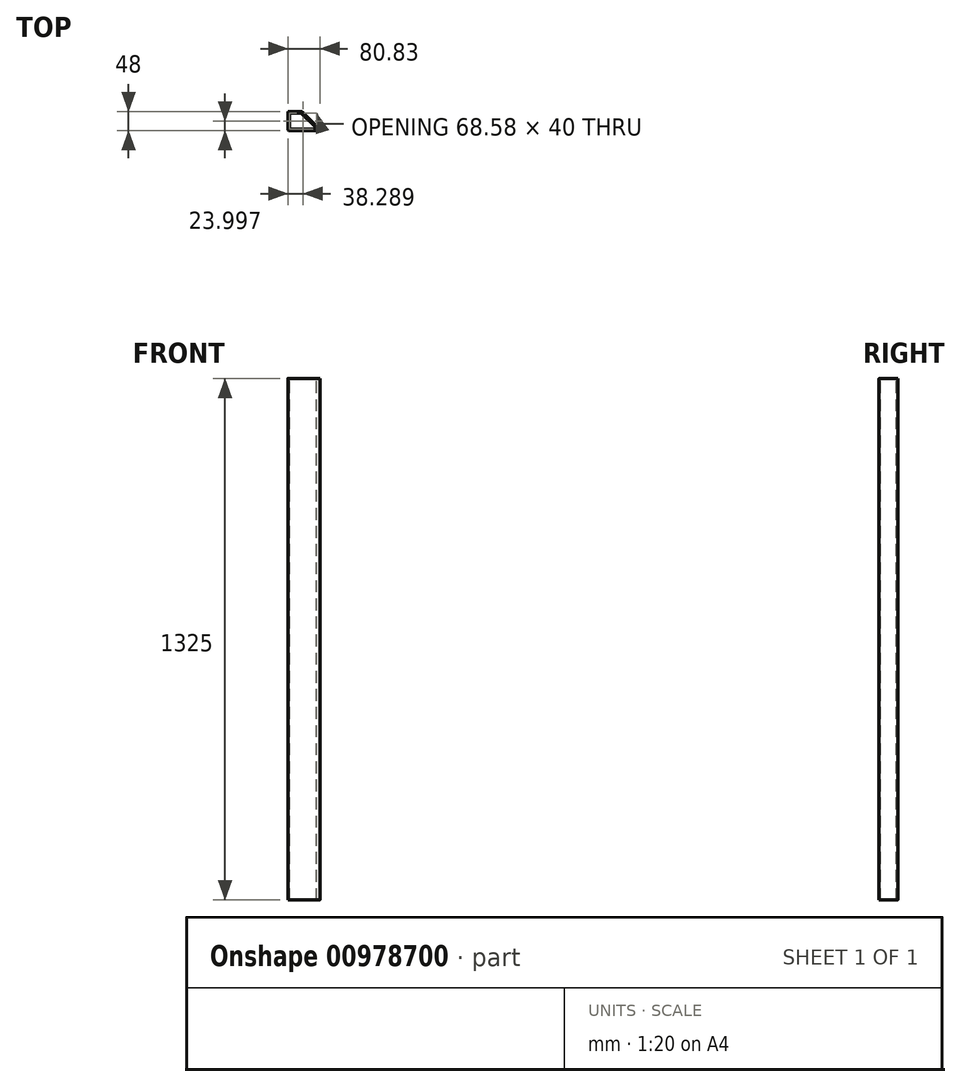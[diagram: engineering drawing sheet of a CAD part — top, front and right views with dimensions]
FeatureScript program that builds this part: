
annotation { "Feature Type Name" : "Feature", "Feature Type Description" : "" }
export const myFeature = defineFeature(function(context is Context, id is Id, definition is map)
    precondition{}
    {
        {
            var Q0;
            Q0=qCreatedBy(makeId("Top.planeOp"),FACE);
            var sketch = newSketch(context, id + "F0", { "sketchPlane" : qUnion([Q0])});
            skLineSegment(sketch, "E0", {"start": v(-67.3, 49.35) * mm, "end": v(-35.7, 49.35) * mm});
            skLineSegment(sketch, "E1", {"start": v(-32.17, 47.88) * mm, "end": v(10.95, 4.76) * mm});
            skLineSegment(sketch, "E2", {"start": v(9.54, 1.35) * mm, "end": v(-67.3, 1.35) * mm});
            skLineSegment(sketch, "E3", {"start": v(-69.3, 3.35) * mm, "end": v(-69.3, 47.35) * mm});
            skLineSegment(sketch, "E4.0", {"start": v(-64.3, 45.35) * mm, "end": v(-36.12, 45.35) * mm});
            skLineSegment(sketch, "E4.1", {"start": v(-65.3, 6.35) * mm, "end": v(-65.3, 44.35) * mm});
            skLineSegment(sketch, "E4.2", {"start": v(2.3, 5.35) * mm, "end": v(-64.3, 5.35) * mm});
            skLineSegment(sketch, "E4.3", {"start": v(-34.7, 44.76) * mm, "end": v(3, 7.05) * mm});
            skPoint(sketch, "E5.visualSharp", {"position": v(-33.63, 49.35) * mm});
            skArc(sketch, "E5.filletArc", {"start": v(-32.17, 47.88) * mm, "mid": v(-33.8, 48.97) * mm, "end": v(-35.7, 49.35) * mm});
            skPoint(sketch, "E6.visualSharp", {"position": v(-69.3, 49.35) * mm});
            skArc(sketch, "E6.filletArc", {"start": v(-67.3, 49.35) * mm, "mid": v(-68.7, 48.76) * mm, "end": v(-69.3, 47.35) * mm});
            skPoint(sketch, "E7.visualSharp", {"position": v(-65.3, 45.35) * mm});
            skArc(sketch, "E7.filletArc", {"start": v(-64.3, 45.35) * mm, "mid": v(-65, 45.05) * mm, "end": v(-65.3, 44.35) * mm});
            skPoint(sketch, "E8.visualSharp", {"position": v(-35.3, 45.35) * mm});
            skArc(sketch, "E8.filletArc", {"start": v(-34.7, 44.76) * mm, "mid": v(-35.35, 45.2) * mm, "end": v(-36.12, 45.35) * mm});
            skPoint(sketch, "E9.visualSharp", {"position": v(-69.3, 1.35) * mm});
            skArc(sketch, "E9.filletArc", {"start": v(-69.3, 3.35) * mm, "mid": v(-68.7, 1.93) * mm, "end": v(-67.3, 1.35) * mm});
            skPoint(sketch, "E10.visualSharp", {"position": v(14.37, 1.35) * mm});
            skArc(sketch, "E10.filletArc", {"start": v(9.54, 1.35) * mm, "mid": v(11.38, 2.58) * mm, "end": v(10.95, 4.76) * mm});
            skPoint(sketch, "E11.visualSharp", {"position": v(-65.3, 5.35) * mm});
            skArc(sketch, "E11.filletArc", {"start": v(-65.3, 6.35) * mm, "mid": v(-65, 5.64) * mm, "end": v(-64.3, 5.35) * mm});
            skPoint(sketch, "E12.visualSharp", {"position": v(4.7, 5.35) * mm});
            skArc(sketch, "E12.filletArc", {"start": v(2.3, 5.35) * mm, "mid": v(3.22, 5.96) * mm, "end": v(3, 7.05) * mm});
            skSolve(sketch);
        }
        {
            var Q0;
            Q0=makeQuery(id+"F0.imprint","IMPRINT",FACE,{"disambiguationData":[TD([[makeQuery(id+"F0.imprint","IMPRINT",EDGE,{"derivedFrom":sQuery(id+"F0.wireOp",EDGE,"E0")}),-1.0]])]});
            extrude(context, id + "F1", {"entities" : qUnion([Q0]), "oppositeDirection" : true, "depth" : 1325 * mm, "offsetDistance" : 25 * mm});
        }
    });
